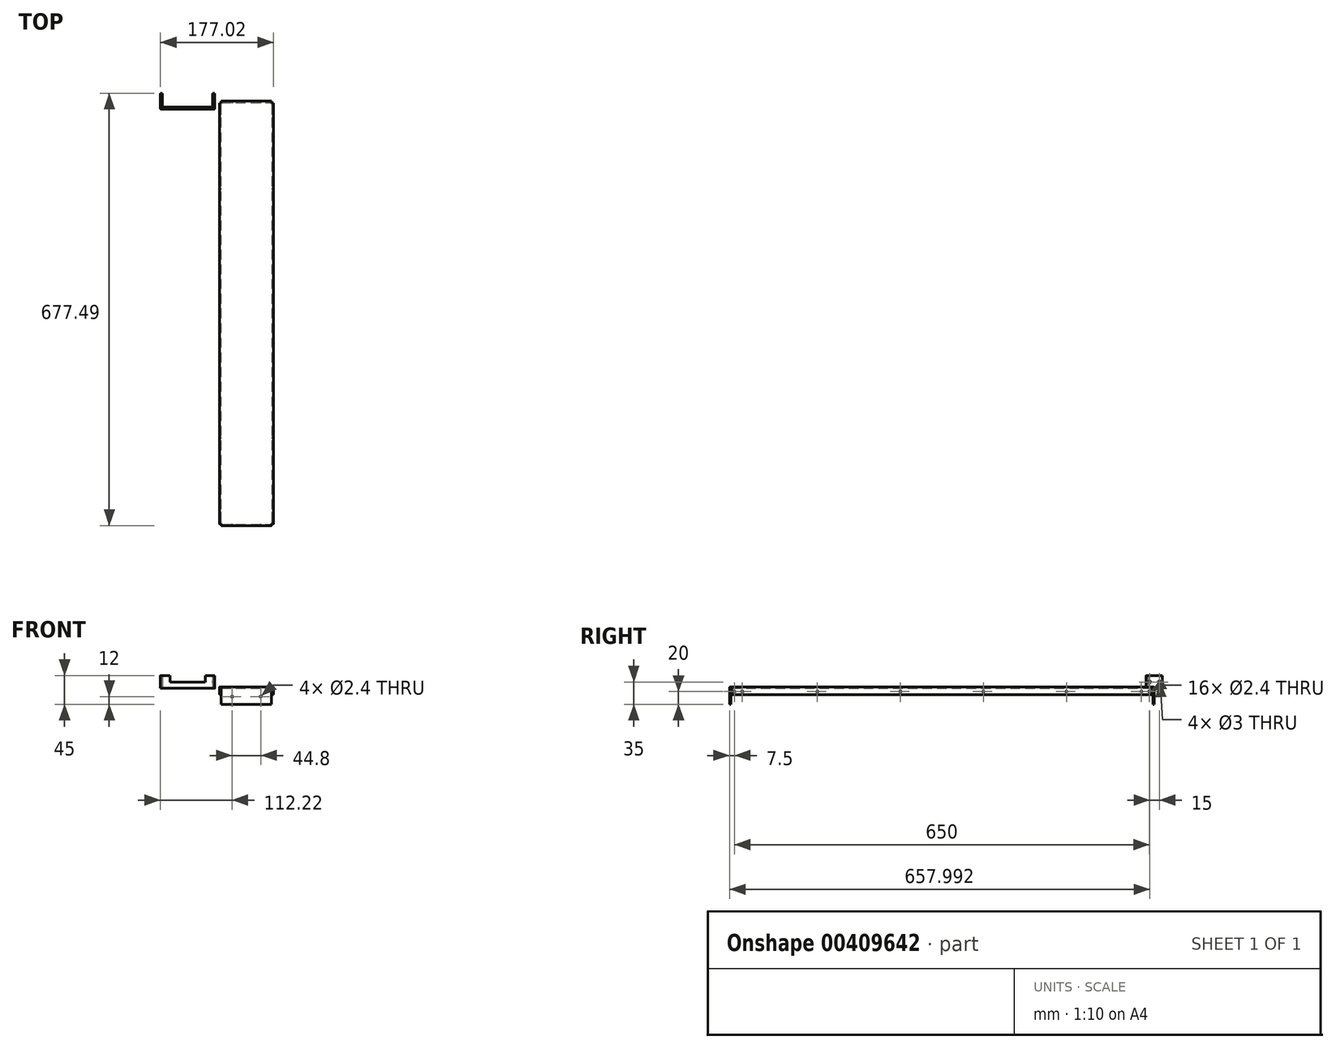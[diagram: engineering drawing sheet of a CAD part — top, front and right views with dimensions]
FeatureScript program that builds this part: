
annotation { "Feature Type Name" : "Feature", "Feature Type Description" : "" }
export const myFeature = defineFeature(function(context is Context, id is Id, definition is map)
    precondition{}
    {
        {
            var Q0;
            Q0=qCreatedBy(makeId("Top.planeOp"),FACE);
            var sketch = newSketch(context, id + "F0", { "sketchPlane" : qUnion([Q0])});
            skLineSegment(sketch, "E0.bottom", {"start": v(42.4, -332.5) * mm, "end": v(-42.4, -332.5) * mm});
            skLineSegment(sketch, "E0.top", {"start": v(42.4, 332.5) * mm, "end": v(-42.4, 332.5) * mm});
            skLineSegment(sketch, "E0.left", {"start": v(42.4, -332.5) * mm, "end": v(42.4, 332.5) * mm});
            skLineSegment(sketch, "E0.right", {"start": v(-42.4, -332.5) * mm, "end": v(-42.4, 332.5) * mm});
            skPoint(sketch, "E0.middle", {"position": v(0, 0) * mm});
            skSolve(sketch);
        }
        {
            var Q0;
            Q0 = qSketchRegion(id + "F0", true);
            extrude(context, id + "F1", {"entities" : qUnion([Q0]), "depth" : 2 * mm});
        }
        {
            var Q0;
            Q0=makeQuery(id+"F1.opExtrude","CAP_FACE",FACE,{"disambiguationData":[OSD([sQuery(id+"F0.wireOp",EDGE,"E0.bottom"),sQuery(id+"F0.wireOp",EDGE,"E0.top"),sQuery(id+"F0.wireOp",EDGE,"E0.left"),sQuery(id+"F0.wireOp",EDGE,"E0.right")])],"isStart":false});
            var sketch = newSketch(context, id + "F2", { "sketchPlane" : qUnion([Q0])});
            skLineSegment(sketch, "E1.bottom", {"start": v(-42.4, 332.5) * mm, "end": v(-39.4, 332.5) * mm});
            skLineSegment(sketch, "E1.top", {"start": v(-42.4, 329.5) * mm, "end": v(-39.4, 329.5) * mm});
            skLineSegment(sketch, "E1.left", {"start": v(-42.4, 332.5) * mm, "end": v(-42.4, 329.5) * mm});
            skLineSegment(sketch, "E1.right", {"start": v(-39.4, 332.5) * mm, "end": v(-39.4, 329.5) * mm});
            skLineSegment(sketch, "E2.bottom", {"start": v(42.4, 332.5) * mm, "end": v(39.4, 332.5) * mm});
            skLineSegment(sketch, "E2.top", {"start": v(42.4, 329.5) * mm, "end": v(39.4, 329.5) * mm});
            skLineSegment(sketch, "E2.left", {"start": v(42.4, 332.5) * mm, "end": v(42.4, 329.5) * mm});
            skLineSegment(sketch, "E2.right", {"start": v(39.4, 332.5) * mm, "end": v(39.4, 329.5) * mm});
            skLineSegment(sketch, "E3.bottom", {"start": v(42.4, -332.5) * mm, "end": v(39.4, -332.5) * mm});
            skLineSegment(sketch, "E3.top", {"start": v(42.4, -329.5) * mm, "end": v(39.4, -329.5) * mm});
            skLineSegment(sketch, "E3.left", {"start": v(42.4, -332.5) * mm, "end": v(42.4, -329.5) * mm});
            skLineSegment(sketch, "E3.right", {"start": v(39.4, -332.5) * mm, "end": v(39.4, -329.5) * mm});
            skLineSegment(sketch, "E4.bottom", {"start": v(-42.4, -332.5) * mm, "end": v(-39.4, -332.5) * mm});
            skLineSegment(sketch, "E4.top", {"start": v(-42.4, -329.5) * mm, "end": v(-39.4, -329.5) * mm});
            skLineSegment(sketch, "E4.left", {"start": v(-42.4, -332.5) * mm, "end": v(-42.4, -329.5) * mm});
            skLineSegment(sketch, "E4.right", {"start": v(-39.4, -332.5) * mm, "end": v(-39.4, -329.5) * mm});
            skSolve(sketch);
        }
        {
            var Q0;
            Q0 = qSketchRegion(id + "F2", true);
            extrude(context, id + "F3", {"entities" : qUnion([Q0]), "operationType" : NewBodyOperationType.REMOVE, "oppositeDirection" : true, "depth" : 2 * mm});
        }
        {
            var Q0;
            Q0=makeQuery(id+"F1.opExtrude","CAP_FACE",FACE,{"disambiguationData":[OSD([sQuery(id+"F0.wireOp",EDGE,"E0.bottom"),sQuery(id+"F0.wireOp",EDGE,"E0.top"),sQuery(id+"F0.wireOp",EDGE,"E0.left"),sQuery(id+"F0.wireOp",EDGE,"E0.right")])],"isStart":true});
            var sketch = newSketch(context, id + "F4", { "sketchPlane" : qUnion([Q0])});
            skLineSegment(sketch, "E5.bottom", {"start": v(-39.4, -332.5) * mm, "end": v(39.4, -332.5) * mm});
            skLineSegment(sketch, "E5.top", {"start": v(-39.4, -330.5) * mm, "end": v(39.4, -330.5) * mm});
            skLineSegment(sketch, "E5.left", {"start": v(-39.4, -330.5) * mm, "end": v(-39.4, -332.5) * mm});
            skLineSegment(sketch, "E5.right", {"start": v(39.4, -330.5) * mm, "end": v(39.4, -332.5) * mm});
            skLineSegment(sketch, "E6.bottom", {"start": v(-42.4, -329.5) * mm, "end": v(-40.4, -329.5) * mm});
            skLineSegment(sketch, "E6.top", {"start": v(-42.4, 329.5) * mm, "end": v(-40.4, 329.5) * mm});
            skLineSegment(sketch, "E6.left", {"start": v(-42.4, -329.5) * mm, "end": v(-42.4, 329.5) * mm});
            skLineSegment(sketch, "E6.right", {"start": v(-40.4, -329.5) * mm, "end": v(-40.4, 329.5) * mm});
            skLineSegment(sketch, "E7.bottom", {"start": v(-39.4, 332.5) * mm, "end": v(39.4, 332.5) * mm});
            skLineSegment(sketch, "E7.top", {"start": v(-39.4, 330.5) * mm, "end": v(39.4, 330.5) * mm});
            skLineSegment(sketch, "E7.left", {"start": v(-39.4, 332.5) * mm, "end": v(-39.4, 330.5) * mm});
            skLineSegment(sketch, "E7.right", {"start": v(39.4, 332.5) * mm, "end": v(39.4, 330.5) * mm});
            skLineSegment(sketch, "E8.bottom", {"start": v(42.4, 329.5) * mm, "end": v(40.4, 329.5) * mm});
            skLineSegment(sketch, "E8.top", {"start": v(42.4, -329.5) * mm, "end": v(40.4, -329.5) * mm});
            skLineSegment(sketch, "E8.left", {"start": v(42.4, 329.5) * mm, "end": v(42.4, -329.5) * mm});
            skLineSegment(sketch, "E8.right", {"start": v(40.4, 329.5) * mm, "end": v(40.4, -329.5) * mm});
            skSolve(sketch);
        }
        {
            var Q0;
            Q0=makeQuery(id+"F4.imprint","IMPRINT",FACE,{"disambiguationData":[TD([[makeQuery(id+"F4.imprint","IMPRINT",EDGE,{"derivedFrom":sQuery(id+"F4.wireOp",EDGE,"E7.bottom")}),1.0]])]});
            var Q1;
            Q1=makeQuery(id+"F4.imprint","IMPRINT",FACE,{"disambiguationData":[TD([[makeQuery(id+"F4.imprint","IMPRINT",EDGE,{"derivedFrom":sQuery(id+"F4.wireOp",EDGE,"E5.bottom")}),-1.0]])]});
            extrude(context, id + "F5", {"entities" : qUnion([Q0, Q1]), "operationType" : NewBodyOperationType.ADD, "depth" : 25 * mm});
        }
        {
            var Q0;
            Q0=makeQuery(id+"F4.imprint","IMPRINT",FACE,{"disambiguationData":[TD([[makeQuery(id+"F4.imprint","IMPRINT",EDGE,{"derivedFrom":sQuery(id+"F4.wireOp",EDGE,"E6.bottom")}),1.0]])]});
            var Q1;
            Q1=makeQuery(id+"F4.imprint","IMPRINT",FACE,{"disambiguationData":[TD([[makeQuery(id+"F4.imprint","IMPRINT",EDGE,{"derivedFrom":sQuery(id+"F4.wireOp",EDGE,"E8.bottom")}),1.0]])]});
            extrude(context, id + "F6", {"entities" : qUnion([Q0, Q1]), "operationType" : NewBodyOperationType.ADD, "depth" : 10 * mm});
        }
        {
            var Q0;
            Q0=makeQuery(id+"F1.opExtrude","CAP_EDGE",EDGE,{"disambiguationData":[OSD([sQuery(id+"F0.wireOp",EDGE,"E0.top")])],"isStart":false});
            var Q1;
            Q1=makeQuery(id+"F1.opExtrude","CAP_EDGE",EDGE,{"disambiguationData":[OSD([sQuery(id+"F0.wireOp",EDGE,"E0.right")])],"isStart":false});
            var Q2;
            Q2=makeQuery(id+"F5.opExtrude","CAP_EDGE",EDGE,{"disambiguationData":[OSD([sQuery(id+"F4.wireOp",EDGE,"E5.top")])],"isStart":true});
            var Q3;
            Q3=makeQuery(id+"F5.opExtrude","CAP_EDGE",EDGE,{"disambiguationData":[OSD([sQuery(id+"F4.wireOp",EDGE,"E6.right")])],"isStart":true});
            var Q4;
            Q4=makeQuery(id+"F5.opExtrude","CAP_EDGE",EDGE,{"disambiguationData":[OSD([sQuery(id+"F4.wireOp",EDGE,"E8.right")])],"isStart":true});
            var Q5;
            Q5=makeQuery(id+"F1.opExtrude","CAP_EDGE",EDGE,{"disambiguationData":[OSD([sQuery(id+"F0.wireOp",EDGE,"E0.left")])],"isStart":false});
            var Q6;
            Q6=makeQuery(id+"F1.opExtrude","CAP_EDGE",EDGE,{"disambiguationData":[OSD([sQuery(id+"F0.wireOp",EDGE,"E0.bottom")])],"isStart":false});
            var Q7;
            Q7=makeQuery(id+"F5.opExtrude","CAP_EDGE",EDGE,{"disambiguationData":[OSD([sQuery(id+"F4.wireOp",EDGE,"E7.top")])],"isStart":true});
            fillet(context, id + "F7", {"entities" : qUnion([Q0, Q1, Q2, Q3, Q4, Q5, Q6, Q7]), "radius" : 1 * mm, "tangentPropagation" : true, "allowEdgeOverflow" : false});
        }
        {
            var Q0;
            Q0=makeQuery(id+"F5.boolean.opBoolean","MERGE",FACE,{"derivedFrom":[makeQuery(id+"F1.opExtrude","SWEPT_FACE",FACE,{"disambiguationData":[OSD([sQuery(id+"F0.wireOp",EDGE,"E0.top")])]}),makeQuery(id+"F5.opExtrude","SWEPT_FACE",FACE,{"disambiguationData":[OSD([sQuery(id+"F4.wireOp",EDGE,"E5.bottom")])]})]});
            var sketch = newSketch(context, id + "F8", { "sketchPlane" : qUnion([Q0])});
            skCircle(sketch, "E9", {"center": v(-22.4, -13) * mm, "radius": 1.2 * mm});
            skCircle(sketch, "E10", {"center": v(22.4, -13) * mm, "radius": 1.2 * mm});
            skSolve(sketch);
        }
        {
            var Q0;
            Q0 = qSketchRegion(id + "F8", true);
            extrude(context, id + "F9", {"entities" : qUnion([Q0]), "operationType" : NewBodyOperationType.REMOVE, "endBound" : BoundingType.THROUGH_ALL, "oppositeDirection" : true, "depth" : 25 * mm});
        }
        {
            var Q0;
            Q0=makeQuery(id+"F6.boolean.opBoolean","MERGE",FACE,{"derivedFrom":[makeQuery(id+"F1.opExtrude","SWEPT_FACE",FACE,{"disambiguationData":[OSD([sQuery(id+"F0.wireOp",EDGE,"E0.left")])]}),makeQuery(id+"F6.opExtrude","SWEPT_FACE",FACE,{"disambiguationData":[OSD([sQuery(id+"F4.wireOp",EDGE,"E8.left")])]})]});
            var sketch = newSketch(context, id + "F10", { "sketchPlane" : qUnion([Q0])});
            skCircle(sketch, "E11", {"center": v(325, -5) * mm, "radius": 1.2 * mm});
            skCircle(sketch, "E12.1.0.0", {"center": v(195, -5) * mm, "radius": 1.2 * mm});
            skCircle(sketch, "E12.2.0.0", {"center": v(65, -5) * mm, "radius": 1.2 * mm});
            skCircle(sketch, "E12.3.0.0", {"center": v(-65, -5) * mm, "radius": 1.2 * mm});
            skCircle(sketch, "E12.4.0.0", {"center": v(-195, -5) * mm, "radius": 1.2 * mm});
            skCircle(sketch, "E12.5.0.0", {"center": v(-325, -5) * mm, "radius": 1.2 * mm});
            skLineSegment(sketch, "E12.direction1", {"start": v(325, -5) * mm, "end": v(195, -5) * mm, "construction": true});
            skCircle(sketch, "E13", {"center": v(312.5, -5) * mm, "radius": 1.2 * mm});
            skCircle(sketch, "E14", {"center": v(-312.5, -5) * mm, "radius": 1.2 * mm});
            skSolve(sketch);
        }
        {
            var Q0;
            Q0 = qSketchRegion(id + "F10", true);
            extrude(context, id + "F11", {"entities" : qUnion([Q0]), "operationType" : NewBodyOperationType.REMOVE, "endBound" : BoundingType.THROUGH_ALL, "oppositeDirection" : true, "depth" : 25 * mm});
        }
        {
            var Q0;
            Q0=qCreatedBy(makeId("Top.planeOp"),FACE);
            var sketch = newSketch(context, id + "F12", { "sketchPlane" : qUnion([Q0])});
            skLineSegment(sketch, "E15.bottom", {"start": v(-131.62, 323) * mm, "end": v(-52.62, 323) * mm});
            skLineSegment(sketch, "E15.top", {"start": v(-131.62, 320) * mm, "end": v(-52.62, 320) * mm});
            skLineSegment(sketch, "E15.left", {"start": v(-131.62, 323) * mm, "end": v(-131.62, 320) * mm});
            skLineSegment(sketch, "E15.right", {"start": v(-52.62, 323) * mm, "end": v(-52.62, 320) * mm});
            skLineSegment(sketch, "E16.bottom", {"start": v(-131.62, 320) * mm, "end": v(-134.62, 320) * mm});
            skLineSegment(sketch, "E16.top", {"start": v(-131.62, 345) * mm, "end": v(-134.62, 345) * mm});
            skLineSegment(sketch, "E16.left", {"start": v(-131.62, 320) * mm, "end": v(-131.62, 345) * mm});
            skLineSegment(sketch, "E16.right", {"start": v(-134.62, 320) * mm, "end": v(-134.62, 345) * mm});
            skLineSegment(sketch, "E17.bottom", {"start": v(-52.62, 320) * mm, "end": v(-49.62, 320) * mm});
            skLineSegment(sketch, "E17.top", {"start": v(-52.62, 345) * mm, "end": v(-49.62, 345) * mm});
            skLineSegment(sketch, "E17.left", {"start": v(-52.62, 320) * mm, "end": v(-52.62, 345) * mm});
            skLineSegment(sketch, "E17.right", {"start": v(-49.62, 320) * mm, "end": v(-49.62, 345) * mm});
            skSolve(sketch);
        }
        {
            var Q0;
            Q0 = qSketchRegion(id + "F12", true);
            extrude(context, id + "F13", {"entities" : qUnion([Q0]), "depth" : 20 * mm});
        }
        {
            var Q0;
            Q0=makeQuery(id+"F13.opExtrude","SWEPT_FACE",FACE,{"disambiguationData":[OSD([sQuery(id+"F12.wireOp",EDGE,"E16.right")])]});
            var sketch = newSketch(context, id + "F14", { "sketchPlane" : qUnion([Q0])});
            skCircle(sketch, "E18", {"center": v(-325.5, 10) * mm, "radius": 1.5 * mm});
            skCircle(sketch, "E19", {"center": v(-340.5, 10) * mm, "radius": 1.5 * mm});
            skSolve(sketch);
        }
        {
            var Q0;
            Q0 = qSketchRegion(id + "F14", true);
            extrude(context, id + "F15", {"entities" : qUnion([Q0]), "operationType" : NewBodyOperationType.REMOVE, "endBound" : BoundingType.THROUGH_ALL, "oppositeDirection" : true, "depth" : 25 * mm});
        }
        {
            var Q0;
            Q0=makeQuery(id+"F13.opExtrude","SWEPT_EDGE",EDGE,{"disambiguationData":[OSD([sQuery(id+"F12.wireOp",EDGE,"E17.bottom"),sQuery(id+"F12.wireOp",EDGE,"E17.right")])]});
            var Q1;
            Q1=makeQuery(id+"F13.opExtrude","SWEPT_EDGE",EDGE,{"disambiguationData":[OSD([sQuery(id+"F12.wireOp",EDGE,"E15.bottom"),sQuery(id+"F12.wireOp",EDGE,"E17.left")])]});
            var Q2;
            Q2=makeQuery(id+"F13.opExtrude","SWEPT_EDGE",EDGE,{"disambiguationData":[OSD([sQuery(id+"F12.wireOp",EDGE,"E16.bottom"),sQuery(id+"F12.wireOp",EDGE,"E16.right")])]});
            var Q3;
            Q3=makeQuery(id+"F13.opExtrude","SWEPT_EDGE",EDGE,{"disambiguationData":[OSD([sQuery(id+"F12.wireOp",EDGE,"E15.bottom"),sQuery(id+"F12.wireOp",EDGE,"E16.left")])]});
            fillet(context, id + "F16", {"entities" : qUnion([Q0, Q1, Q2, Q3]), "radius" : 1 * mm, "tangentPropagation" : true, "allowEdgeOverflow" : false});
        }
        {
            var Q0;
            Q0=makeQuery(id+"F13.opExtrude","SWEPT_FACE",FACE,{"disambiguationData":[OSD([sQuery(id+"F12.wireOp",EDGE,"E15.top"),sQuery(id+"F12.wireOp",EDGE,"E16.bottom"),sQuery(id+"F12.wireOp",EDGE,"E17.bottom")])]});
            var sketch = newSketch(context, id + "F17", { "sketchPlane" : qUnion([Q0])});
            skLineSegment(sketch, "E20.bottom", {"start": v(-64.62, 10) * mm, "end": v(-119.62, 10) * mm});
            skLineSegment(sketch, "E20.top", {"start": v(-64.62, 20) * mm, "end": v(-119.62, 20) * mm});
            skLineSegment(sketch, "E20.left", {"start": v(-64.62, 10) * mm, "end": v(-64.62, 20) * mm});
            skLineSegment(sketch, "E20.right", {"start": v(-119.62, 10) * mm, "end": v(-119.62, 20) * mm});
            skPoint(sketch, "E20.middle", {"position": v(-92.12, 15) * mm});
            skSolve(sketch);
        }
        {
            var Q0;
            Q0 = qSketchRegion(id + "F17", true);
            extrude(context, id + "F18", {"entities" : qUnion([Q0]), "operationType" : NewBodyOperationType.REMOVE, "oppositeDirection" : true, "depth" : 3 * mm});
        }
    });
